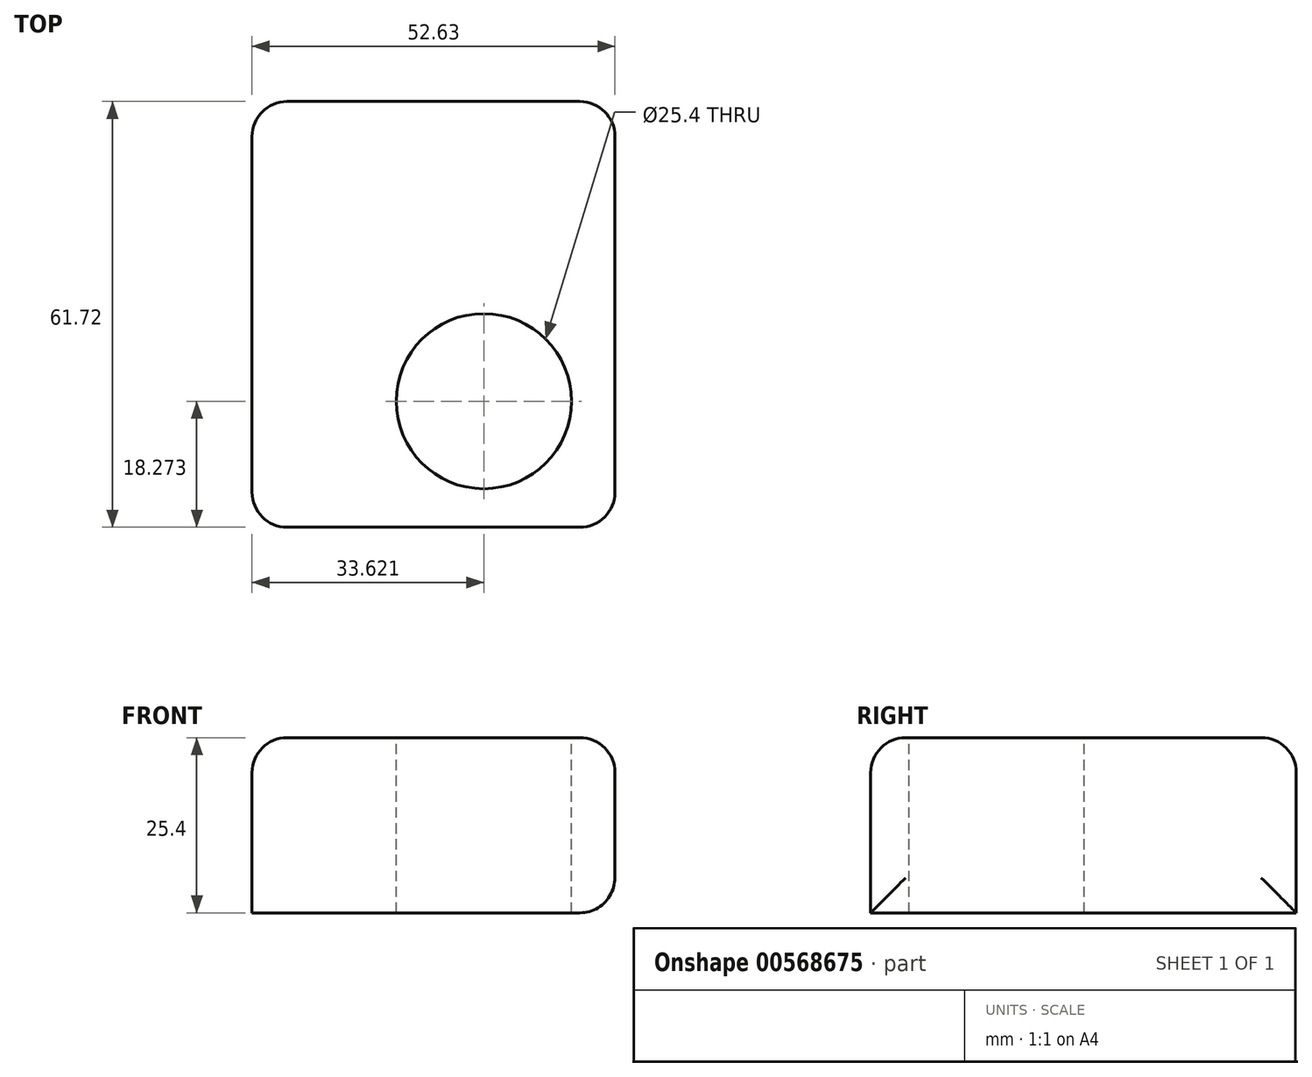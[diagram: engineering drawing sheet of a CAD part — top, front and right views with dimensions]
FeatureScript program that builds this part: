
annotation { "Feature Type Name" : "Feature", "Feature Type Description" : "" }
export const myFeature = defineFeature(function(context is Context, id is Id, definition is map)
    precondition{}
    {
        {
            var Q0;
            Q0=qCreatedBy(makeId("Top.planeOp"),FACE);
            var sketch = newSketch(context, id + "F0", { "sketchPlane" : qUnion([Q0])});
            skLineSegment(sketch, "E0.bottom", {"start": v(-38.23, -45.05) * mm, "end": v(14.4, -45.05) * mm});
            skLineSegment(sketch, "E0.top", {"start": v(-38.23, 16.67) * mm, "end": v(14.4, 16.67) * mm});
            skLineSegment(sketch, "E0.left", {"start": v(-38.23, -45.05) * mm, "end": v(-38.23, 16.67) * mm});
            skLineSegment(sketch, "E0.right", {"start": v(14.4, -45.05) * mm, "end": v(14.4, 16.67) * mm});
            skSolve(sketch);
        }
        {
            var Q0;
            Q0=makeQuery(id+"F0.imprint","IMPRINT",FACE,{"disambiguationData":[TD([[makeQuery(id+"F0.imprint","IMPRINT",EDGE,{"derivedFrom":sQuery(id+"F0.wireOp",EDGE,"E0.bottom")}),1.0]])]});
            extrude(context, id + "F1", {"entities" : qUnion([Q0]), "depth" : 25.4 * mm, "offsetDistance" : 25.4 * mm});
        }
        {
            var Q0;
            Q0=makeQuery(id+"F1.opExtrude","SWEPT_FACE",FACE,{"disambiguationData":[OSD([sQuery(id+"F0.wireOp",EDGE,"E0.right")])]});
            var Q1;
            Q1=makeQuery(id+"F1.opExtrude","CAP_FACE",FACE,{"disambiguationData":[OSD([sQuery(id+"F0.wireOp",EDGE,"E0.bottom"),sQuery(id+"F0.wireOp",EDGE,"E0.top"),sQuery(id+"F0.wireOp",EDGE,"E0.left"),sQuery(id+"F0.wireOp",EDGE,"E0.right")])],"isStart":false});
            var Q2;
            Q2=makeQuery(id+"F1.opExtrude","SWEPT_EDGE",EDGE,{"disambiguationData":[OSD([sQuery(id+"F0.wireOp",EDGE,"E0.top"),sQuery(id+"F0.wireOp",EDGE,"E0.left")])]});
            var Q3;
            Q3=makeQuery(id+"F1.opExtrude","SWEPT_EDGE",EDGE,{"disambiguationData":[OSD([sQuery(id+"F0.wireOp",EDGE,"E0.bottom"),sQuery(id+"F0.wireOp",EDGE,"E0.left")])]});
            fillet(context, id + "F2", {"entities" : qUnion([Q0, Q1, Q2, Q3]), "radius" : 5.08 * mm, "tangentPropagation" : true, "allowEdgeOverflow" : false});
        }
        {
            var Q0;
            Q0=makeQuery(id+"F1.opExtrude","CAP_FACE",FACE,{"disambiguationData":[OSD([sQuery(id+"F0.wireOp",EDGE,"E0.bottom"),sQuery(id+"F0.wireOp",EDGE,"E0.top"),sQuery(id+"F0.wireOp",EDGE,"E0.left"),sQuery(id+"F0.wireOp",EDGE,"E0.right")])],"isStart":false});
            var sketch = newSketch(context, id + "F3", { "sketchPlane" : qUnion([Q0])});
            skPoint(sketch, "E1", {"position": v(-4.6, -26.78) * mm});
            skSolve(sketch);
        }
        {
            var Q0;
            Q0=sQuery(id+"F3.wireOp",VERTEX,"E1");
            var Q1;
            Q1=makeQuery(id+"F1.opExtrude","SWEPT_BODY",BODY,{"disambiguationData":[OSD([sQuery(id+"F0.wireOp",EDGE,"E0.bottom"),sQuery(id+"F0.wireOp",EDGE,"E0.top"),sQuery(id+"F0.wireOp",EDGE,"E0.left"),sQuery(id+"F0.wireOp",EDGE,"E0.right")])]});
            hole(context, id + "F4", {"style" : HoleStyle.SIMPLE, "endStyle" : HoleEndStyle.THROUGH, "holeDiameter" : 25.4 * mm, "isTappedThrough" : true, "tappedDepth" : 12.7 * mm, "tapClearance" : 3, "locations" : qUnion([Q0]), "scope" : qUnion([Q1])});
        }
    });
